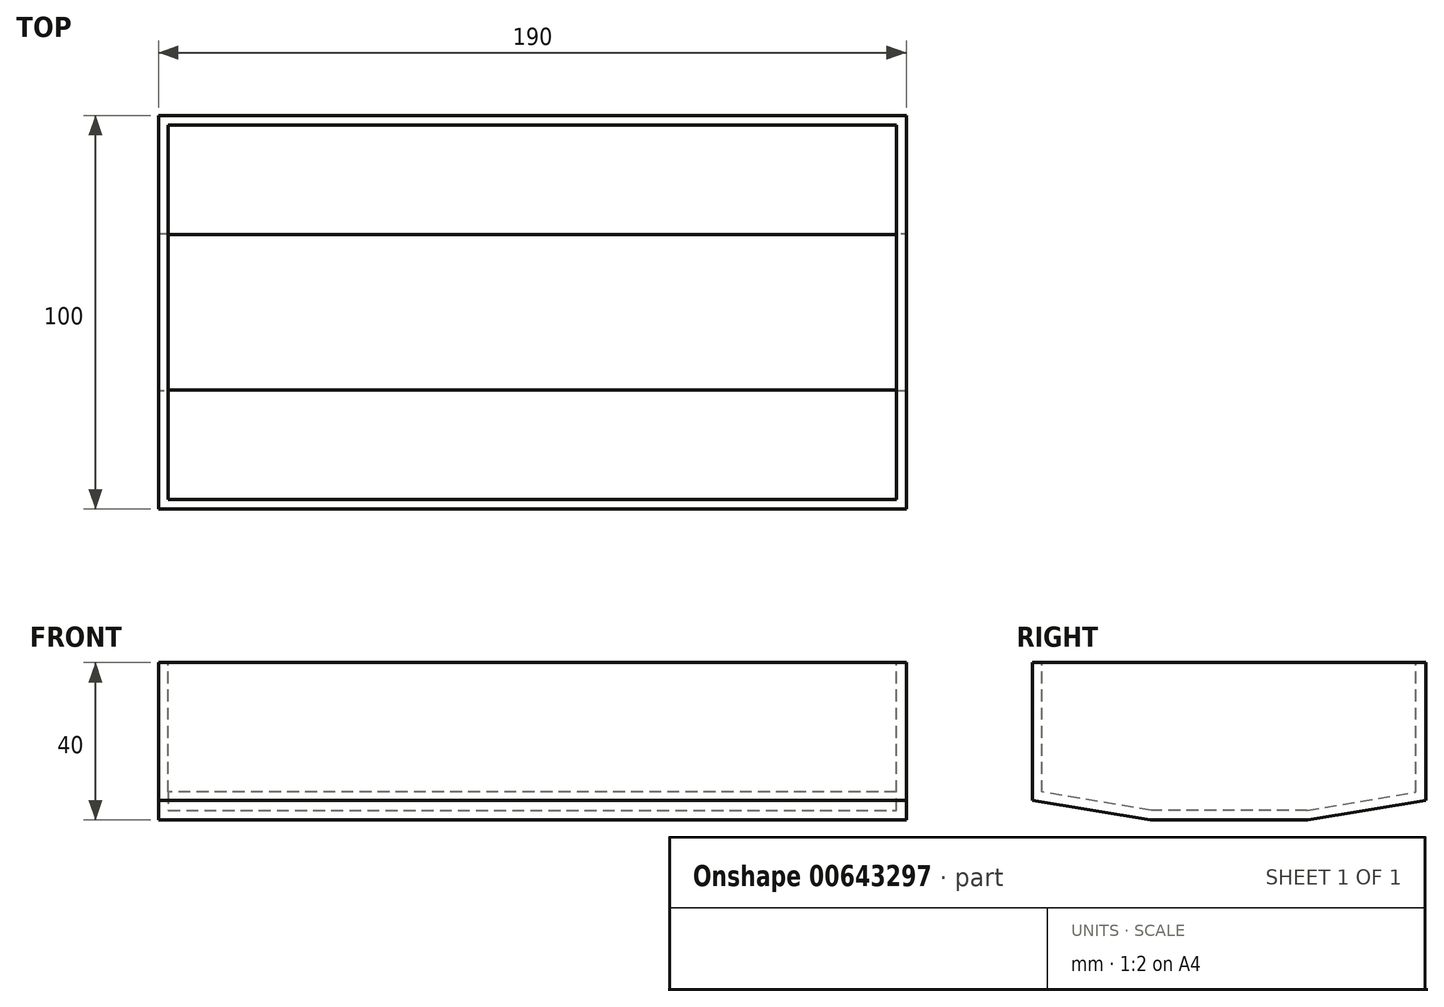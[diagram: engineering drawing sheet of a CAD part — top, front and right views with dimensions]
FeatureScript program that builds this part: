
annotation { "Feature Type Name" : "Feature", "Feature Type Description" : "" }
export const myFeature = defineFeature(function(context is Context, id is Id, definition is map)
    precondition{}
    {
        {
            var Q0;
            Q0=qCreatedBy(makeId("Top.planeOp"),FACE);
            var sketch = newSketch(context, id + "F0", { "sketchPlane" : qUnion([Q0])});
            skLineSegment(sketch, "E0.bottom", {"start": v(95, 50) * mm, "end": v(-95, 50) * mm});
            skLineSegment(sketch, "E0.top", {"start": v(95, -50) * mm, "end": v(-95, -50) * mm});
            skLineSegment(sketch, "E0.left", {"start": v(95, 50) * mm, "end": v(95, -50) * mm});
            skLineSegment(sketch, "E0.right", {"start": v(-95, 50) * mm, "end": v(-95, -50) * mm});
            skPoint(sketch, "E0.middle", {"position": v(0, 0) * mm});
            skSolve(sketch);
        }
        {
            var Q0;
            Q0=makeQuery(id+"F0.imprint","IMPRINT",FACE,{"disambiguationData":[TD([[makeQuery(id+"F0.imprint","IMPRINT",EDGE,{"derivedFrom":sQuery(id+"F0.wireOp",EDGE,"E0.bottom")}),1.0]])]});
            extrude(context, id + "F1", {"entities" : qUnion([Q0]), "oppositeDirection" : true, "depth" : 40 * mm, "offsetDistance" : 25 * mm});
        }
        {
            var Q0;
            Q0=makeQuery(id+"F1.opExtrude","CAP_EDGE",EDGE,{"disambiguationData":[OSD([sQuery(id+"F0.wireOp",EDGE,"E0.bottom")])],"isStart":false});
            var Q1;
            Q1=makeQuery(id+"F1.opExtrude","CAP_EDGE",EDGE,{"disambiguationData":[OSD([sQuery(id+"F0.wireOp",EDGE,"E0.top")])],"isStart":false});
            chamfer(context, id + "F2", {"entities" : qUnion([Q0, Q1]), "chamferType" : ChamferType.TWO_OFFSETS, "width1" : 5 * mm, "oppositeDirection" : false, "width2" : 30 * mm, "tangentPropagation" : true});
        }
        {
            var Q0;
            Q0=makeQuery(id+"F1.opExtrude","CAP_FACE",FACE,{"disambiguationData":[OSD([sQuery(id+"F0.wireOp",EDGE,"E0.bottom"),sQuery(id+"F0.wireOp",EDGE,"E0.top"),sQuery(id+"F0.wireOp",EDGE,"E0.left"),sQuery(id+"F0.wireOp",EDGE,"E0.right")])],"isStart":true});
            shell(context, id + "F3", {"entities" : qUnion([Q0]), "thickness" : 2.5 * mm});
        }
    });
